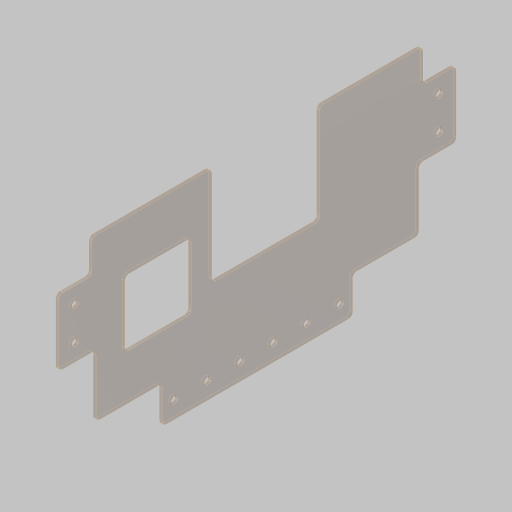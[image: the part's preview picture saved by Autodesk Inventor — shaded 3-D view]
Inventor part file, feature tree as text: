
AUTODESK INVENTOR PART (.ipt)
format: ipt  version: 2023.5 (Build 275446000, 446)  size: 324,096 bytes
history: native  units: in
note: dims shown in document units (in); Inventor stores cm internally (conversion verified against a paired STEP export)
features: sketch x3, extrude x2, fillet x2, projected_geometry x2, hole x1
ambient origin geometry x8: Origin, YZ Plane, XZ Plane, XY Plane, X Axis, Y Axis, Z Axis, Center Point
bodies: Solid1 (feature_tree)
feature tree (10):
  extrude  "Extrusion1"  Depth=12.0in
  fillet  "Fillet1"  Radius=2.0in
  hole  "Hole1"  [1 undecoded]
  extrude  "Extrusion2"  Depth=0.125in
  fillet  "Fillet2"  Radius=0.5in
  sketch  "Sketch1"  dims[d0=6.0in d1=12.0in d2=2.0in]
  sketch  "Sketch2"  dims[d3=3.5in d4=3.0in]
  sketch  "Sketch3"  dims[d5=0.09in d6=0.0in d7=0.125in d8=0.5in d9=0.5in d10=0.5in d11=2.3622in d13=1.0in d14=0.3937in d16=1.0in d18=0.201in d19=0.75in d20=0.385in d21=0.25in d22=0.5635in d23=1.0in d24=0.8108in d25=1.125in d26=3.0in d27=1.125in d28=3.125in d29=0.09in d30=0.0in d31=0.125in d32=4.7244in d34=1.0in d35=0.3937in d37=1.0in d39=3.0in d40=3.25in d41=5.75in d42=1.0in]
  projected_geometry  "Project Cut Edges1"
  projected_geometry  "Project Cut Edges2"
note: 1 required parameter value undecoded (feature->parameter linkage not recoverable at this tier; creation-order binding heuristic only, values carry confidence <= 0.55)
